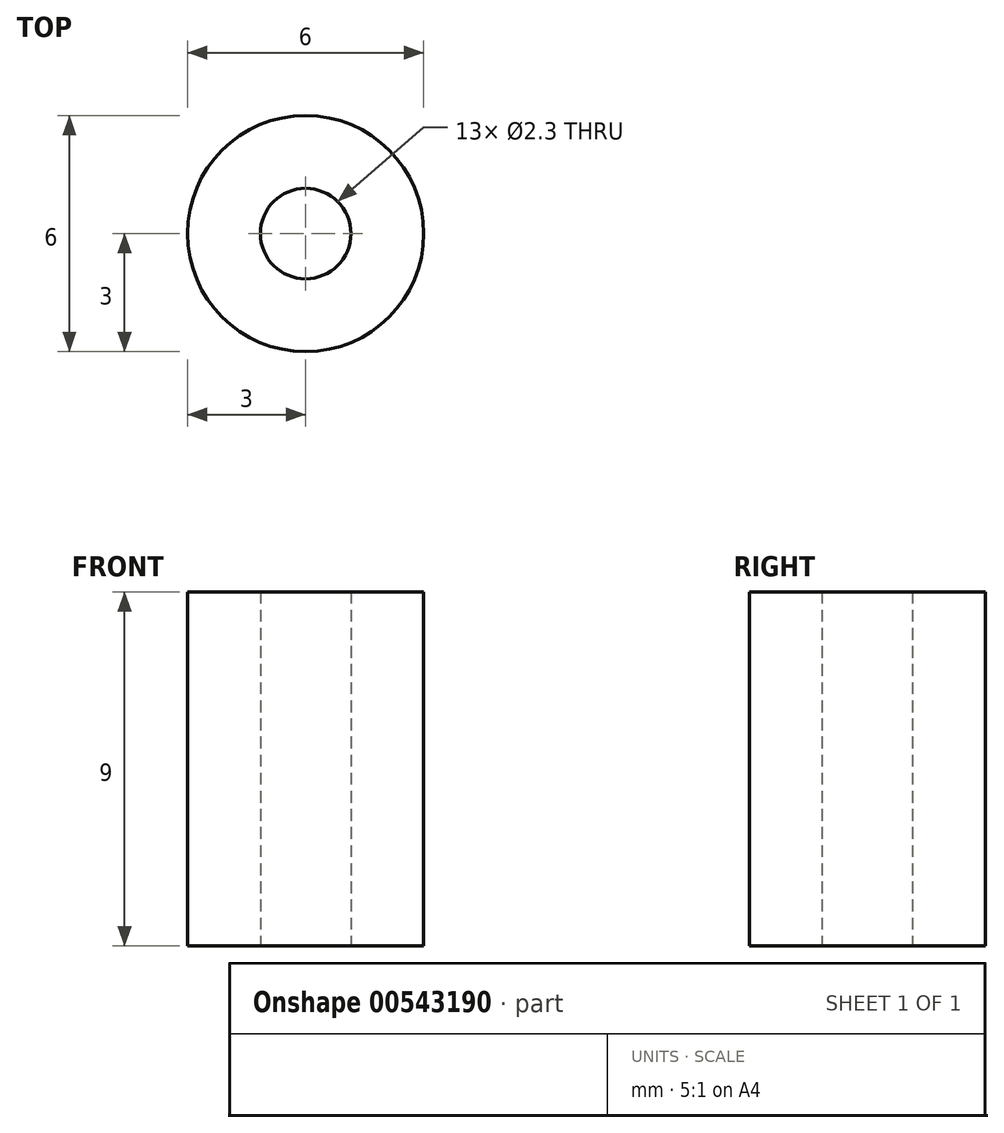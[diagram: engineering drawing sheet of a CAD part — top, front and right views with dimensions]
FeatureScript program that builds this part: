
annotation { "Feature Type Name" : "Feature", "Feature Type Description" : "" }
export const myFeature = defineFeature(function(context is Context, id is Id, definition is map)
    precondition{}
    {
        {
            var Q0;
            Q0=qCreatedBy(makeId("Front.planeOp"),FACE);
            var sketch = newSketch(context, id + "F0", { "sketchPlane" : qUnion([Q0])});
            skLineSegment(sketch, "E0.bottom", {"start": v(1.15, 4.5) * mm, "end": v(-1.15, 4.5) * mm});
            skLineSegment(sketch, "E0.top", {"start": v(1.15, -4.5) * mm, "end": v(-1.15, -4.5) * mm});
            skLineSegment(sketch, "E0.left", {"start": v(1.15, 4.5) * mm, "end": v(1.15, -4.5) * mm});
            skLineSegment(sketch, "E0.right", {"start": v(-1.15, 4.5) * mm, "end": v(-1.15, -4.5) * mm});
            skPoint(sketch, "E0.middle", {"position": v(0, 0) * mm});
            skLineSegment(sketch, "E1.bottom", {"start": v(3, -4.5) * mm, "end": v(-3, -4.5) * mm});
            skLineSegment(sketch, "E1.top", {"start": v(3, 4.5) * mm, "end": v(-3, 4.5) * mm});
            skLineSegment(sketch, "E1.left", {"start": v(3, -4.5) * mm, "end": v(3, 4.5) * mm});
            skLineSegment(sketch, "E1.right", {"start": v(-3, -4.5) * mm, "end": v(-3, 4.5) * mm});
            skLineSegment(sketch, "E2", {"start": v(0, 0) * mm, "end": v(0, 14.21) * mm});
            skPoint(sketch, "E2.endSnap0", {"position": v(0, 4.5) * mm});
            skSolve(sketch);
        }
        {
            var Q0;
            {var subQ0=sQuery(id+"F0.wireOp",EDGE,"E0.right");Q0=makeQuery(id+"F0.imprint","IMPRINT",FACE,{"disambiguationData":[TD([[makeQuery(id+"F0.imprint","IMPRINT",EDGE,{"derivedFrom":subQ0}),-1.0]])]});}
            var Q1;
            Q1=sQuery(id+"F0.wireOp",EDGE,"E2");
            revolve(context, id + "F1", {"entities" : qUnion([Q0]), "axis" : qUnion([Q1]), "revolveType" : RevolveType.FULL});
        }
    });
